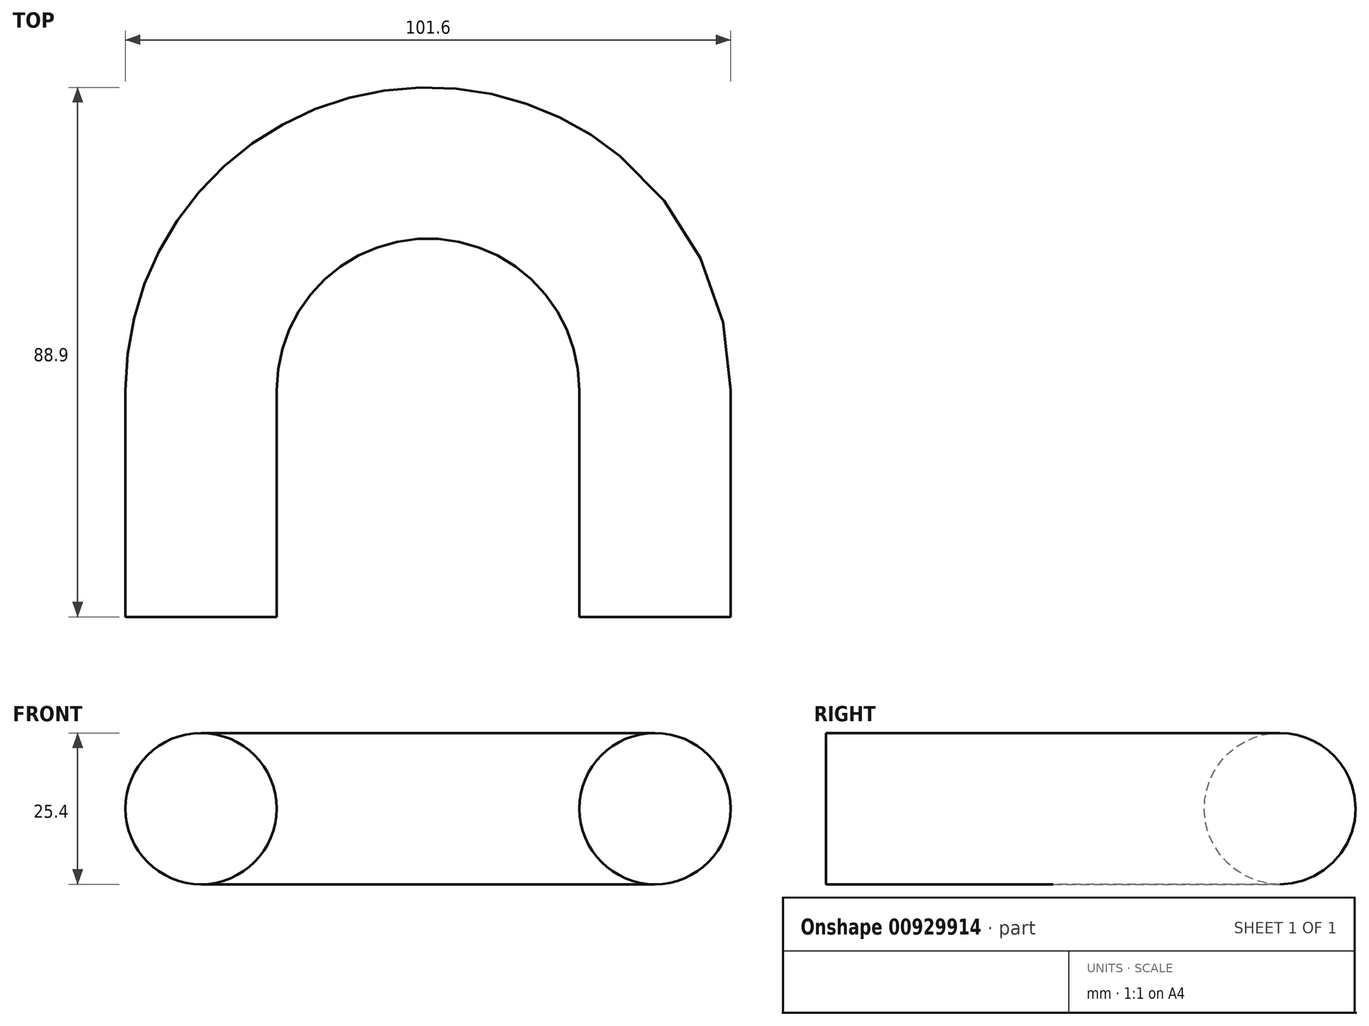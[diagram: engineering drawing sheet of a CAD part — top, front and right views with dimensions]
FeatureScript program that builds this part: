
annotation { "Feature Type Name" : "Feature", "Feature Type Description" : "" }
export const myFeature = defineFeature(function(context is Context, id is Id, definition is map)
    precondition{}
    {
        {
            var Q0;
            Q0=qCreatedBy(makeId("Top.planeOp"),FACE);
            var sketch = newSketch(context, id + "F0", { "sketchPlane" : qUnion([Q0])});
            skLineSegment(sketch, "E0", {"start": v(38.1, 0) * mm, "end": v(38.1, 38.1) * mm});
            skArc(sketch, "E1", {"start": v(38.1, 38.1) * mm, "mid": v(0, 76.2) * mm, "end": v(-38.1, 38.1) * mm});
            skLineSegment(sketch, "E2", {"start": v(-38.1, 38.1) * mm, "end": v(-38.1, 0) * mm});
            skSolve(sketch);
        }
        {
            var Q0;
            Q0=qCreatedBy(makeId("Front.planeOp"),FACE);
            var sketch = newSketch(context, id + "F1", { "sketchPlane" : qUnion([Q0])});
            skCircle(sketch, "E3", {"center": v(38.1, 0) * mm, "radius": 12.7 * mm});
            skSolve(sketch);
        }
        {
            var Q0;
            Q0=makeQuery(id+"F1.imprint","IMPRINT",FACE,{"disambiguationData":[TD([[makeQuery(id+"F1.imprint","IMPRINT",EDGE,{"derivedFrom":sQuery(id+"F1.wireOp",EDGE,"E3")}),1.0]])]});
            var Q1;
            Q1 = qConstructionFilter(qBodyType(qCreatedBy(id + "F0" ,EDGE), BodyType.WIRE), ConstructionObject.NO);
            sweep(context, id + "F2", {"profiles" : qUnion([Q0]), "path" : qUnion([Q1])});
        }
    });
